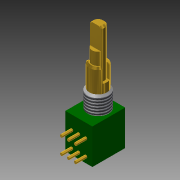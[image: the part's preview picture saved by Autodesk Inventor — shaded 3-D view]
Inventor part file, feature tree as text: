
AUTODESK INVENTOR PART (.ipt)
format: ipt  version: 2016 (Build 200138000, 138)  size: 178,688 bytes
history: native  units: mm
features: extrude x7, sketch x7, chamfer x1, thread x1
ambient origin geometry x8: Origin, YZ Plane, XZ Plane, XY Plane, X Axis, Y Axis, Z Axis, Center Point
bodies: Solid1 (feature_tree)
feature tree (16):
  extrude  "Extrusion1"  Depth=7.7mm
  extrude  "Extrusion2"  Depth=5.5mm
  extrude  "Extrusion3"  Depth=10.0mm
  extrude  "Extrusion4"  Depth=5.0mm
  extrude  "Extrusion5"  Depth=2.0mm
  extrude  "Extrusion6"  Depth=2.0mm
  chamfer  "Chamfer1"  Distance=6.5mm
  extrude  "Extrusion7"  Depth=10.0mm TaperAngle=0.0deg
  thread  "Thread1"  [1 undecoded]
  sketch  "Sketch1"  dims[d0=7.7mm d1=3.85mm]
  sketch  "Sketch2"  dims[d2=3.85mm d3=5.5mm]
  sketch  "Sketch3"  dims[d4=10.0mm d5=0.0mm d6=6.0mm]
  sketch  "Sketch4"  dims[d7=5.0mm d8=0.0mm d9=5.0mm]
  sketch  "Sketch5"  dims[d10=6.5mm d11=0.0mm d12=2.0mm]
  sketch  "Sketch6"  dims[d13=4.0mm d14=2.0mm d15=6.5mm d16=0.0mm]
  sketch  "Sketch7"  dims[d17=3.5mm d18=21.0mm d19=0.0mm d21=2.5mm d22=2.0mm d23=2.0mm d24=2.0mm d25=6.0mm d26=0.0mm d27=0.5mm d28=2.0mm d29=45.0deg d30=0.8mm d31=3.8mm d32=4.5mm d33=2.0mm d34=2.0mm d37=3.85mm d38=1.7mm d39=3.0mm d40=0.0mm d41=10.0mm d42=0.0mm]
note: 1 required parameter value undecoded (feature->parameter linkage not recoverable at this tier; creation-order binding heuristic only, values carry confidence <= 0.55)
